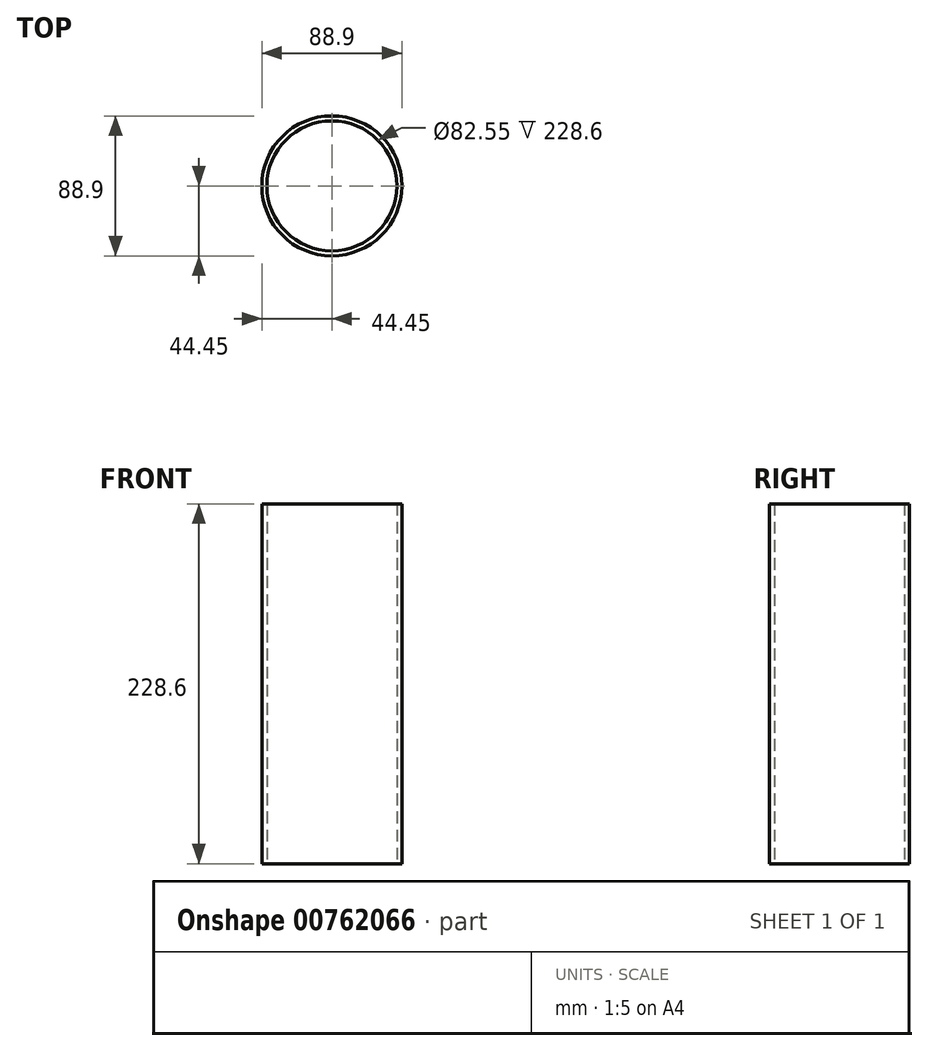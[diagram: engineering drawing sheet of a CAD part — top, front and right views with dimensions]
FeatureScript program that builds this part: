
annotation { "Feature Type Name" : "Feature", "Feature Type Description" : "" }
export const myFeature = defineFeature(function(context is Context, id is Id, definition is map)
    precondition{}
    {
        {
            var Q0;
            Q0=qCreatedBy(makeId("Top.planeOp"),FACE);
            var sketch = newSketch(context, id + "F0", { "sketchPlane" : qUnion([Q0])});
            skCircle(sketch, "E0", {"center": v(0, 0) * mm, "radius": 44.45 * mm});
            skCircle(sketch, "E1", {"center": v(0, 0) * mm, "radius": 41.28 * mm});
            skSolve(sketch);
        }
        {
            var Q0;
            Q0 = qSketchRegion(id + "F0", true);
            extrude(context, id + "F1", {"entities" : qUnion([Q0]), "depth" : 228.6 * mm, "offsetDistance" : 25 * mm});
        }
        {
            var Q0;
            Q0=qCreatedBy(makeId("Top.planeOp"),FACE);
            cPlane(context, id + "F2", {"entities" : qUnion([Q0]), "cplaneType" : CPlaneType.OFFSET, "offset" : 152.4 * mm, "width" : 150 * mm, "height" : 150 * mm});
        }
    });
